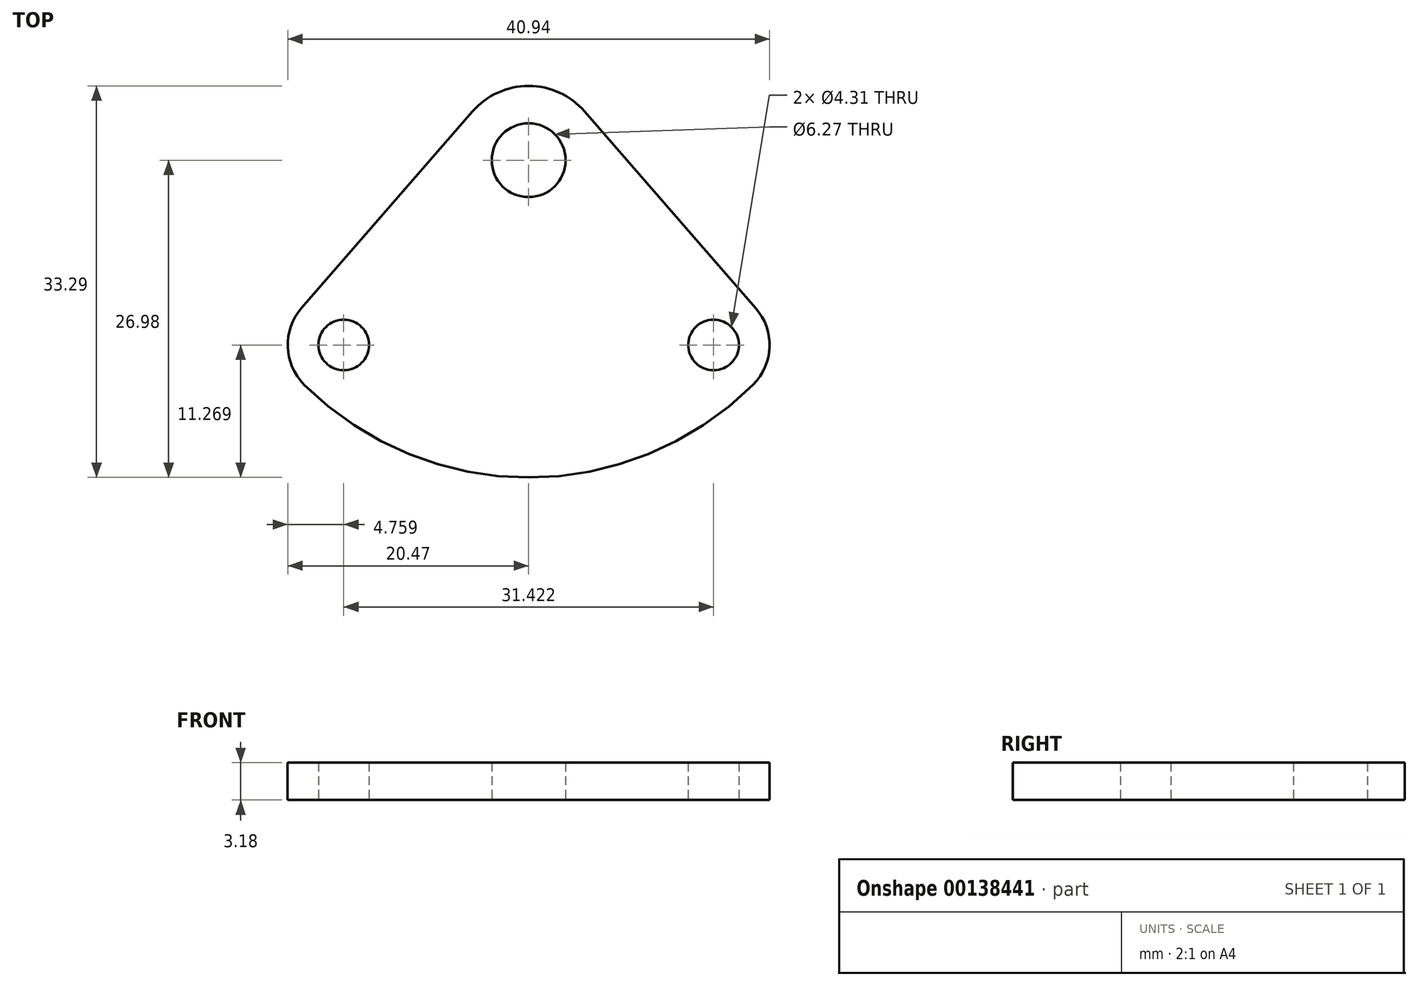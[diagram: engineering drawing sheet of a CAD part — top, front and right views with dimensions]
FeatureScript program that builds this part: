
annotation { "Feature Type Name" : "Feature", "Feature Type Description" : "" }
export const myFeature = defineFeature(function(context is Context, id is Id, definition is map)
    precondition{}
    {
        {
            var Q0;
            Q0=qCreatedBy(makeId("Top.planeOp"),FACE);
            var sketch = newSketch(context, id + "F0", { "sketchPlane" : qUnion([Q0])});
            skCircle(sketch, "E0", {"center": v(0, 0) * mm, "radius": 17.46 * mm, "construction": true});
            skArc(sketch, "E1", {"start": v(4.76, 4.14) * mm, "mid": v(0, 6.31) * mm, "end": v(-4.76, 4.14) * mm});
            skLineSegment(sketch, "E2", {"start": v(0, 0) * mm, "end": v(0, -15.71) * mm, "construction": true});
            skLineSegment(sketch, "E3", {"start": v(-15.71, -15.71) * mm, "end": v(15.71, -15.71) * mm, "construction": true});
            skLineSegment(sketch, "E4", {"start": v(0, 0) * mm, "end": v(15.71, -15.71) * mm, "construction": true});
            skCircle(sketch, "E5", {"center": v(-15.71, -15.71) * mm, "radius": 2.15 * mm});
            skCircle(sketch, "E6", {"center": v(15.71, -15.71) * mm, "radius": 2.15 * mm});
            skArc(sketch, "E7", {"start": v(-19.3, -12.59) * mm, "mid": v(-20.47, -15.88) * mm, "end": v(-19.08, -19.08) * mm});
            skArc(sketch, "E8", {"start": v(19.08, -19.08) * mm, "mid": v(20.47, -15.88) * mm, "end": v(19.3, -12.59) * mm});
            skLineSegment(sketch, "E9", {"start": v(-19.3, -12.59) * mm, "end": v(-4.76, 4.14) * mm});
            skLineSegment(sketch, "E10", {"start": v(4.76, 4.14) * mm, "end": v(19.3, -12.59) * mm});
            skCircle(sketch, "E11", {"center": v(0, 0) * mm, "radius": 3.14 * mm});
            skArc(sketch, "E12", {"start": v(-19.08, -19.08) * mm, "mid": v(0, -26.98) * mm, "end": v(19.08, -19.08) * mm});
            skSolve(sketch);
        }
        {
            var Q0;
            Q0 = qSketchRegion(id + "F0", true);
            extrude(context, id + "F1", {"entities" : qUnion([Q0]), "depth" : 3.17 * mm});
        }
    });
